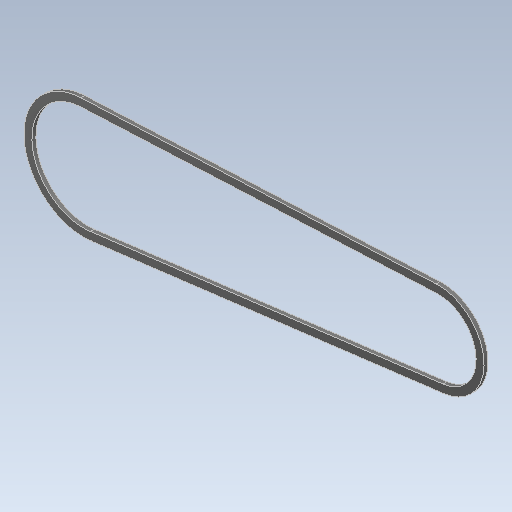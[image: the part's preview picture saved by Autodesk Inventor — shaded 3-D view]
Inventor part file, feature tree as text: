
AUTODESK INVENTOR PART (.ipt)
format: ipt  version: 2021 (Build 250183000, 183)  size: 97,792 bytes
history: mixed  units: mm
features: other x1, extrude x1, imported_body x1
ambient origin geometry x8: Origin, YZ Plane, XZ Plane, XY Plane, X Axis, Y Axis, Z Axis, Center Point
bodies: Body1 (imported_parasolid)
feature tree (3):
  other  "Sólido1"
  extrude  "Extrude-Thin1"  [1 undecoded]
  imported_body  NMx_Import_Brep_tag  [imported B-rep: ~10 faces, bbox_mm=[455.81797, 170.033257, 5.0]]
note: 1 required parameter value undecoded (feature->parameter linkage not recoverable at this tier; creation-order binding heuristic only, values carry confidence <= 0.55)
